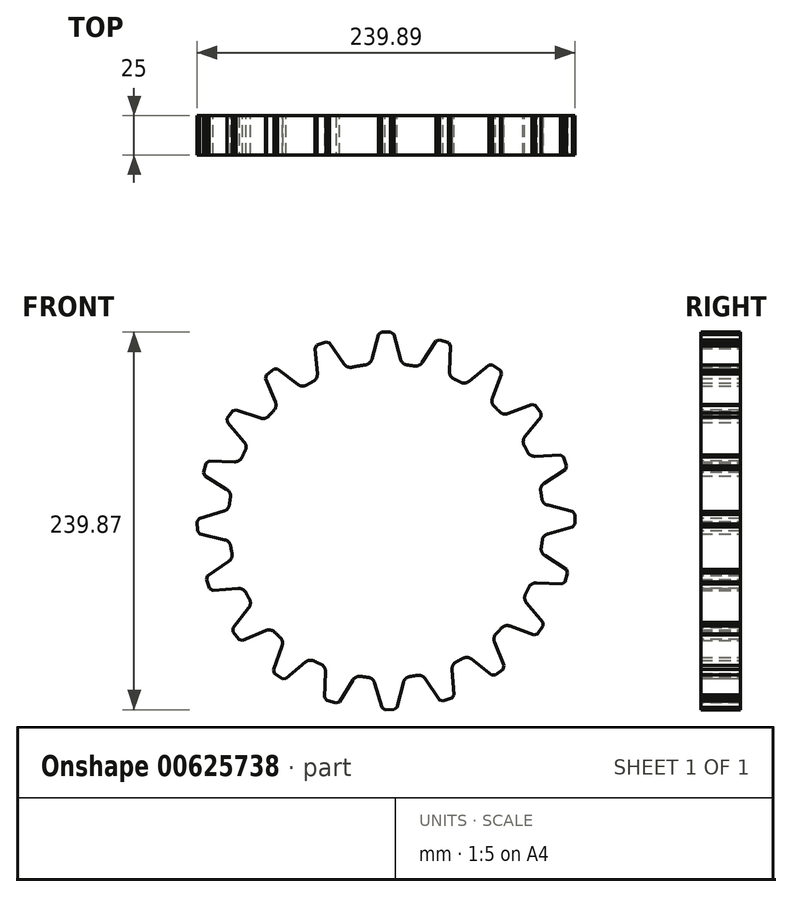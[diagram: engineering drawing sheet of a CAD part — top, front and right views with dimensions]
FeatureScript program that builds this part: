
annotation { "Feature Type Name" : "Feature", "Feature Type Description" : "" }
export const myFeature = defineFeature(function(context is Context, id is Id, definition is map)
    precondition{}
    {
        {
            var Q0;
            Q0=qCreatedBy(makeId("Front.planeOp"),FACE);
            var sketch = newSketch(context, id + "F0", { "sketchPlane" : qUnion([Q0])});
            skCircle(sketch, "E0", {"center": v(0, 0) * mm, "radius": 100 * mm});
            skCircle(sketch, "E1", {"center": v(0, 0) * mm, "radius": 120 * mm, "construction": true});
            skLineSegment(sketch, "E2", {"start": v(0, 0) * mm, "end": v(0, 133.33) * mm, "construction": true});
            skLineSegment(sketch, "E3", {"start": v(-4.5, 119.92) * mm, "end": v(-9.97, 99.5) * mm});
            skLineSegment(sketch, "E4.MirrorCS", {"start": v(4.5, 119.92) * mm, "end": v(9.97, 99.5) * mm});
            skLineSegment(sketch, "E5", {"start": v(-4.5, 119.92) * mm, "end": v(4.5, 119.92) * mm});
            skLineSegment(sketch, "E6.1.0", {"start": v(41.13, 112.73) * mm, "end": v(40.06, 91.62) * mm});
            skLineSegment(sketch, "E6.1.1", {"start": v(32.56, 115.5) * mm, "end": v(41.13, 112.73) * mm});
            skLineSegment(sketch, "E6.1.2", {"start": v(32.56, 115.5) * mm, "end": v(21.09, 97.75) * mm});
            skLineSegment(sketch, "E6.2.0", {"start": v(73.78, 94.64) * mm, "end": v(66.28, 74.88) * mm});
            skLineSegment(sketch, "E6.2.1", {"start": v(66.48, 99.9) * mm, "end": v(73.78, 94.64) * mm});
            skLineSegment(sketch, "E6.2.2", {"start": v(66.48, 99.9) * mm, "end": v(50.1, 86.54) * mm});
            skLineSegment(sketch, "E6.3.0", {"start": v(99.29, 67.4) * mm, "end": v(86.08, 50.9) * mm});
            skLineSegment(sketch, "E6.3.1", {"start": v(93.96, 74.64) * mm, "end": v(99.29, 67.4) * mm});
            skLineSegment(sketch, "E6.3.2", {"start": v(93.96, 74.64) * mm, "end": v(74.27, 66.96) * mm});
            skLineSegment(sketch, "E6.4.0", {"start": v(115.2, 33.62) * mm, "end": v(97.55, 21.98) * mm});
            skLineSegment(sketch, "E6.4.1", {"start": v(112.35, 42.16) * mm, "end": v(115.2, 33.62) * mm});
            skLineSegment(sketch, "E6.4.2", {"start": v(112.35, 42.16) * mm, "end": v(91.25, 40.9) * mm});
            skLineSegment(sketch, "E6.5.0", {"start": v(119.95, -3.4) * mm, "end": v(99.59, -9.06) * mm});
            skLineSegment(sketch, "E6.5.1", {"start": v(119.87, 5.6) * mm, "end": v(119.95, -3.4) * mm});
            skLineSegment(sketch, "E6.5.2", {"start": v(119.87, 5.6) * mm, "end": v(99.4, 10.88) * mm});
            skLineSegment(sketch, "E6.6.0", {"start": v(113.1, -40.1) * mm, "end": v(91.99, -39.22) * mm});
            skLineSegment(sketch, "E6.6.1", {"start": v(115.8, -31.5) * mm, "end": v(113.1, -40.1) * mm});
            skLineSegment(sketch, "E6.6.2", {"start": v(115.8, -31.5) * mm, "end": v(97.94, -20.19) * mm});
            skLineSegment(sketch, "E6.7.0", {"start": v(95.31, -72.9) * mm, "end": v(75.49, -65.59) * mm});
            skLineSegment(sketch, "E6.7.1", {"start": v(100.51, -65.56) * mm, "end": v(95.31, -72.9) * mm});
            skLineSegment(sketch, "E6.7.2", {"start": v(100.51, -65.56) * mm, "end": v(87, -49.3) * mm});
            skLineSegment(sketch, "E6.8.0", {"start": v(68.3, -98.67) * mm, "end": v(51.68, -85.6) * mm});
            skLineSegment(sketch, "E6.8.1", {"start": v(75.5, -93.27) * mm, "end": v(68.3, -98.67) * mm});
            skLineSegment(sketch, "E6.8.2", {"start": v(75.5, -93.27) * mm, "end": v(67.64, -73.65) * mm});
            skLineSegment(sketch, "E6.9.0", {"start": v(34.68, -114.88) * mm, "end": v(22.88, -97.35) * mm});
            skLineSegment(sketch, "E6.9.1", {"start": v(43.2, -111.96) * mm, "end": v(34.68, -114.88) * mm});
            skLineSegment(sketch, "E6.9.2", {"start": v(43.2, -111.96) * mm, "end": v(41.74, -90.87) * mm});
            skLineSegment(sketch, "E6.10.0", {"start": v(-2.3, -119.98) * mm, "end": v(-8.14, -99.67) * mm});
            skLineSegment(sketch, "E6.10.1", {"start": v(6.7, -119.81) * mm, "end": v(-2.3, -119.98) * mm});
            skLineSegment(sketch, "E6.10.2", {"start": v(6.7, -119.81) * mm, "end": v(11.8, -99.3) * mm});
            skLineSegment(sketch, "E6.11.0", {"start": v(-39.05, -113.47) * mm, "end": v(-38.37, -92.35) * mm});
            skLineSegment(sketch, "E6.11.1", {"start": v(-30.44, -116.08) * mm, "end": v(-39.05, -113.47) * mm});
            skLineSegment(sketch, "E6.11.2", {"start": v(-30.44, -116.08) * mm, "end": v(-19.29, -98.12) * mm});
            skLineSegment(sketch, "E6.12.0", {"start": v(-72.03, -95.98) * mm, "end": v(-64.89, -76.09) * mm});
            skLineSegment(sketch, "E6.12.1", {"start": v(-64.63, -101.1) * mm, "end": v(-72.03, -95.98) * mm});
            skLineSegment(sketch, "E6.12.2", {"start": v(-64.63, -101.1) * mm, "end": v(-48.5, -87.45) * mm});
            skLineSegment(sketch, "E6.13.0", {"start": v(-98.03, -69.2) * mm, "end": v(-85.13, -52.47) * mm});
            skLineSegment(sketch, "E6.13.1", {"start": v(-92.57, -76.36) * mm, "end": v(-98.03, -69.2) * mm});
            skLineSegment(sketch, "E6.13.2", {"start": v(-92.57, -76.36) * mm, "end": v(-73.03, -68.31) * mm});
            skLineSegment(sketch, "E6.14.0", {"start": v(-114.56, -35.73) * mm, "end": v(-97.13, -23.77) * mm});
            skLineSegment(sketch, "E6.14.1", {"start": v(-111.56, -44.22) * mm, "end": v(-114.56, -35.73) * mm});
            skLineSegment(sketch, "E6.14.2", {"start": v(-111.56, -44.22) * mm, "end": v(-90.49, -42.57) * mm});
            skLineSegment(sketch, "E6.15.0", {"start": v(-120, 1.2) * mm, "end": v(-99.74, 7.22) * mm});
            skLineSegment(sketch, "E6.15.1", {"start": v(-119.75, -7.8) * mm, "end": v(-120, 1.2) * mm});
            skLineSegment(sketch, "E6.15.2", {"start": v(-119.75, -7.8) * mm, "end": v(-99.19, -12.7) * mm});
            skLineSegment(sketch, "E6.16.0", {"start": v(-113.82, 38) * mm, "end": v(-92.7, 37.52) * mm});
            skLineSegment(sketch, "E6.16.1", {"start": v(-116.35, 29.37) * mm, "end": v(-113.82, 38) * mm});
            skLineSegment(sketch, "E6.16.2", {"start": v(-116.35, 29.37) * mm, "end": v(-98.3, 18.38) * mm});
            skLineSegment(sketch, "E6.17.0", {"start": v(-96.64, 71.14) * mm, "end": v(-76.68, 64.19) * mm});
            skLineSegment(sketch, "E6.17.1", {"start": v(-101.7, 63.7) * mm, "end": v(-96.64, 71.14) * mm});
            skLineSegment(sketch, "E6.17.2", {"start": v(-101.7, 63.7) * mm, "end": v(-87.9, 47.7) * mm});
            skLineSegment(sketch, "E6.18.0", {"start": v(-70.1, 97.4) * mm, "end": v(-53.25, 84.64) * mm});
            skLineSegment(sketch, "E6.18.1", {"start": v(-77.2, 91.87) * mm, "end": v(-70.1, 97.4) * mm});
            skLineSegment(sketch, "E6.18.2", {"start": v(-77.2, 91.87) * mm, "end": v(-68.98, 72.4) * mm});
            skLineSegment(sketch, "E6.19.0", {"start": v(-36.78, 114.22) * mm, "end": v(-24.66, 96.91) * mm});
            skLineSegment(sketch, "E6.19.1", {"start": v(-45.24, 111.14) * mm, "end": v(-36.78, 114.22) * mm});
            skLineSegment(sketch, "E6.19.2", {"start": v(-45.24, 111.14) * mm, "end": v(-43.4, 90.1) * mm});
            skLineSegment(sketch, "E6.anchor1", {"start": v(0, 0) * mm, "end": v(-9.97, 99.5) * mm, "construction": true});
            skLineSegment(sketch, "E6.anchor2", {"start": v(0, 0) * mm, "end": v(-43.4, 90.1) * mm, "construction": true});
            skSolve(sketch);
        }
        {
            var Q0;
            Q0 = qSketchRegion(id + "F0", true);
            extrude(context, id + "F1", {"entities" : qUnion([Q0]), "depth" : 25 * mm, "offsetDistance" : 25 * mm});
        }
        {
            var Q0;
            Q0=makeQuery(id+"F1.opExtrude","SWEPT_EDGE",EDGE,{"disambiguationData":[OSD([sQuery(id+"F0.wireOp",EDGE,"E4.MirrorCS"),sQuery(id+"F0.wireOp",EDGE,"E5")])]});
            var Q1;
            Q1=makeQuery(id+"F1.opExtrude","SWEPT_EDGE",EDGE,{"disambiguationData":[OSD([sQuery(id+"F0.wireOp",EDGE,"E3"),sQuery(id+"F0.wireOp",EDGE,"E5")])]});
            var Q2;
            Q2=makeQuery(id+"F1.opExtrude","SWEPT_EDGE",EDGE,{"disambiguationData":[OSD([sQuery(id+"F0.wireOp",EDGE,"E6.1.1"),sQuery(id+"F0.wireOp",EDGE,"E6.1.2")])]});
            var Q3;
            Q3=makeQuery(id+"F1.opExtrude","SWEPT_EDGE",EDGE,{"disambiguationData":[OSD([sQuery(id+"F0.wireOp",EDGE,"E6.1.0"),sQuery(id+"F0.wireOp",EDGE,"E6.1.1")])]});
            var Q4;
            Q4=makeQuery(id+"F1.opExtrude","SWEPT_EDGE",EDGE,{"disambiguationData":[OSD([sQuery(id+"F0.wireOp",EDGE,"E6.2.1"),sQuery(id+"F0.wireOp",EDGE,"E6.2.2")])]});
            var Q5;
            Q5=makeQuery(id+"F1.opExtrude","SWEPT_EDGE",EDGE,{"disambiguationData":[OSD([sQuery(id+"F0.wireOp",EDGE,"E6.2.0"),sQuery(id+"F0.wireOp",EDGE,"E6.2.1")])]});
            var Q6;
            Q6=makeQuery(id+"F1.opExtrude","SWEPT_EDGE",EDGE,{"disambiguationData":[OSD([sQuery(id+"F0.wireOp",EDGE,"E6.3.0"),sQuery(id+"F0.wireOp",EDGE,"E6.3.1")])]});
            var Q7;
            Q7=makeQuery(id+"F1.opExtrude","SWEPT_EDGE",EDGE,{"disambiguationData":[OSD([sQuery(id+"F0.wireOp",EDGE,"E6.3.1"),sQuery(id+"F0.wireOp",EDGE,"E6.3.2")])]});
            var Q8;
            Q8=makeQuery(id+"F1.opExtrude","SWEPT_EDGE",EDGE,{"disambiguationData":[OSD([sQuery(id+"F0.wireOp",EDGE,"E6.4.1"),sQuery(id+"F0.wireOp",EDGE,"E6.4.2")])]});
            var Q9;
            Q9=makeQuery(id+"F1.opExtrude","SWEPT_EDGE",EDGE,{"disambiguationData":[OSD([sQuery(id+"F0.wireOp",EDGE,"E6.4.0"),sQuery(id+"F0.wireOp",EDGE,"E6.4.1")])]});
            var Q10;
            Q10=makeQuery(id+"F1.opExtrude","SWEPT_EDGE",EDGE,{"disambiguationData":[OSD([sQuery(id+"F0.wireOp",EDGE,"E6.5.1"),sQuery(id+"F0.wireOp",EDGE,"E6.5.2")])]});
            var Q11;
            Q11=makeQuery(id+"F1.opExtrude","SWEPT_EDGE",EDGE,{"disambiguationData":[OSD([sQuery(id+"F0.wireOp",EDGE,"E6.5.0"),sQuery(id+"F0.wireOp",EDGE,"E6.5.1")])]});
            var Q12;
            Q12=makeQuery(id+"F1.opExtrude","SWEPT_EDGE",EDGE,{"disambiguationData":[OSD([sQuery(id+"F0.wireOp",EDGE,"E6.6.1"),sQuery(id+"F0.wireOp",EDGE,"E6.6.2")])]});
            var Q13;
            Q13=makeQuery(id+"F1.opExtrude","SWEPT_EDGE",EDGE,{"disambiguationData":[OSD([sQuery(id+"F0.wireOp",EDGE,"E6.6.0"),sQuery(id+"F0.wireOp",EDGE,"E6.6.1")])]});
            var Q14;
            Q14=makeQuery(id+"F1.opExtrude","SWEPT_EDGE",EDGE,{"disambiguationData":[OSD([sQuery(id+"F0.wireOp",EDGE,"E6.7.1"),sQuery(id+"F0.wireOp",EDGE,"E6.7.2")])]});
            var Q15;
            Q15=makeQuery(id+"F1.opExtrude","SWEPT_EDGE",EDGE,{"disambiguationData":[OSD([sQuery(id+"F0.wireOp",EDGE,"E6.7.0"),sQuery(id+"F0.wireOp",EDGE,"E6.7.1")])]});
            var Q16;
            Q16=makeQuery(id+"F1.opExtrude","SWEPT_EDGE",EDGE,{"disambiguationData":[OSD([sQuery(id+"F0.wireOp",EDGE,"E6.8.1"),sQuery(id+"F0.wireOp",EDGE,"E6.8.2")])]});
            var Q17;
            Q17=makeQuery(id+"F1.opExtrude","SWEPT_EDGE",EDGE,{"disambiguationData":[OSD([sQuery(id+"F0.wireOp",EDGE,"E6.8.0"),sQuery(id+"F0.wireOp",EDGE,"E6.8.1")])]});
            var Q18;
            Q18=makeQuery(id+"F1.opExtrude","SWEPT_EDGE",EDGE,{"disambiguationData":[OSD([sQuery(id+"F0.wireOp",EDGE,"E6.9.1"),sQuery(id+"F0.wireOp",EDGE,"E6.9.2")])]});
            var Q19;
            Q19=makeQuery(id+"F1.opExtrude","SWEPT_EDGE",EDGE,{"disambiguationData":[OSD([sQuery(id+"F0.wireOp",EDGE,"E6.9.0"),sQuery(id+"F0.wireOp",EDGE,"E6.9.1")])]});
            var Q20;
            Q20=makeQuery(id+"F1.opExtrude","SWEPT_EDGE",EDGE,{"disambiguationData":[OSD([sQuery(id+"F0.wireOp",EDGE,"E6.10.1"),sQuery(id+"F0.wireOp",EDGE,"E6.10.2")])]});
            var Q21;
            Q21=makeQuery(id+"F1.opExtrude","SWEPT_EDGE",EDGE,{"disambiguationData":[OSD([sQuery(id+"F0.wireOp",EDGE,"E6.10.0"),sQuery(id+"F0.wireOp",EDGE,"E6.10.1")])]});
            var Q22;
            Q22=makeQuery(id+"F1.opExtrude","SWEPT_EDGE",EDGE,{"disambiguationData":[OSD([sQuery(id+"F0.wireOp",EDGE,"E6.11.1"),sQuery(id+"F0.wireOp",EDGE,"E6.11.2")])]});
            var Q23;
            Q23=makeQuery(id+"F1.opExtrude","SWEPT_EDGE",EDGE,{"disambiguationData":[OSD([sQuery(id+"F0.wireOp",EDGE,"E6.11.0"),sQuery(id+"F0.wireOp",EDGE,"E6.11.1")])]});
            var Q24;
            Q24=makeQuery(id+"F1.opExtrude","SWEPT_EDGE",EDGE,{"disambiguationData":[OSD([sQuery(id+"F0.wireOp",EDGE,"E6.12.1"),sQuery(id+"F0.wireOp",EDGE,"E6.12.2")])]});
            var Q25;
            Q25=makeQuery(id+"F1.opExtrude","SWEPT_EDGE",EDGE,{"disambiguationData":[OSD([sQuery(id+"F0.wireOp",EDGE,"E6.12.0"),sQuery(id+"F0.wireOp",EDGE,"E6.12.1")])]});
            var Q26;
            Q26=makeQuery(id+"F1.opExtrude","SWEPT_EDGE",EDGE,{"disambiguationData":[OSD([sQuery(id+"F0.wireOp",EDGE,"E6.13.1"),sQuery(id+"F0.wireOp",EDGE,"E6.13.2")])]});
            var Q27;
            Q27=makeQuery(id+"F1.opExtrude","SWEPT_EDGE",EDGE,{"disambiguationData":[OSD([sQuery(id+"F0.wireOp",EDGE,"E6.13.0"),sQuery(id+"F0.wireOp",EDGE,"E6.13.1")])]});
            var Q28;
            Q28=makeQuery(id+"F1.opExtrude","SWEPT_EDGE",EDGE,{"disambiguationData":[OSD([sQuery(id+"F0.wireOp",EDGE,"E6.14.1"),sQuery(id+"F0.wireOp",EDGE,"E6.14.2")])]});
            var Q29;
            Q29=makeQuery(id+"F1.opExtrude","SWEPT_EDGE",EDGE,{"disambiguationData":[OSD([sQuery(id+"F0.wireOp",EDGE,"E6.14.0"),sQuery(id+"F0.wireOp",EDGE,"E6.14.1")])]});
            var Q30;
            Q30=makeQuery(id+"F1.opExtrude","SWEPT_EDGE",EDGE,{"disambiguationData":[OSD([sQuery(id+"F0.wireOp",EDGE,"E6.15.1"),sQuery(id+"F0.wireOp",EDGE,"E6.15.2")])]});
            var Q31;
            Q31=makeQuery(id+"F1.opExtrude","SWEPT_EDGE",EDGE,{"disambiguationData":[OSD([sQuery(id+"F0.wireOp",EDGE,"E6.15.0"),sQuery(id+"F0.wireOp",EDGE,"E6.15.1")])]});
            var Q32;
            Q32=makeQuery(id+"F1.opExtrude","SWEPT_EDGE",EDGE,{"disambiguationData":[OSD([sQuery(id+"F0.wireOp",EDGE,"E6.16.1"),sQuery(id+"F0.wireOp",EDGE,"E6.16.2")])]});
            var Q33;
            Q33=makeQuery(id+"F1.opExtrude","SWEPT_EDGE",EDGE,{"disambiguationData":[OSD([sQuery(id+"F0.wireOp",EDGE,"E6.16.0"),sQuery(id+"F0.wireOp",EDGE,"E6.16.1")])]});
            var Q34;
            Q34=makeQuery(id+"F1.opExtrude","SWEPT_EDGE",EDGE,{"disambiguationData":[OSD([sQuery(id+"F0.wireOp",EDGE,"E6.17.1"),sQuery(id+"F0.wireOp",EDGE,"E6.17.2")])]});
            var Q35;
            Q35=makeQuery(id+"F1.opExtrude","SWEPT_EDGE",EDGE,{"disambiguationData":[OSD([sQuery(id+"F0.wireOp",EDGE,"E6.17.0"),sQuery(id+"F0.wireOp",EDGE,"E6.17.1")])]});
            var Q36;
            Q36=makeQuery(id+"F1.opExtrude","SWEPT_EDGE",EDGE,{"disambiguationData":[OSD([sQuery(id+"F0.wireOp",EDGE,"E6.18.1"),sQuery(id+"F0.wireOp",EDGE,"E6.18.2")])]});
            var Q37;
            Q37=makeQuery(id+"F1.opExtrude","SWEPT_EDGE",EDGE,{"disambiguationData":[OSD([sQuery(id+"F0.wireOp",EDGE,"E6.18.0"),sQuery(id+"F0.wireOp",EDGE,"E6.18.1")])]});
            var Q38;
            Q38=makeQuery(id+"F1.opExtrude","SWEPT_EDGE",EDGE,{"disambiguationData":[OSD([sQuery(id+"F0.wireOp",EDGE,"E6.19.1"),sQuery(id+"F0.wireOp",EDGE,"E6.19.2")])]});
            var Q39;
            Q39=makeQuery(id+"F1.opExtrude","SWEPT_EDGE",EDGE,{"disambiguationData":[OSD([sQuery(id+"F0.wireOp",EDGE,"E6.19.0"),sQuery(id+"F0.wireOp",EDGE,"E6.19.1")])]});
            chamfer(context, id + "F2", {"entities" : qUnion([Q0, Q1, Q2, Q3, Q4, Q5, Q6, Q7, Q8, Q9, Q10, Q11, Q12, Q13, Q14, Q15, Q16, Q17, Q18, Q19, Q20, Q21, Q22, Q23, Q24, Q25, Q26, Q27, Q28, Q29, Q30, Q31, Q32, Q33, Q34, Q35, Q36, Q37, Q38, Q39]), "width" : 2 * mm, "tangentPropagation" : true});
        }
        {
            var Q0;
            Q0=makeQuery(id+"F1.opExtrude","SWEPT_EDGE",EDGE,{"disambiguationData":[OSD([sQuery(id+"F0.wireOp",EDGE,"E0"),sQuery(id+"F0.wireOp",EDGE,"E6.18.0")])]});
            var Q1;
            Q1=makeQuery(id+"F1.opExtrude","SWEPT_EDGE",EDGE,{"disambiguationData":[OSD([sQuery(id+"F0.wireOp",EDGE,"E0"),sQuery(id+"F0.wireOp",EDGE,"E6.19.2")])]});
            var Q2;
            Q2=makeQuery(id+"F1.opExtrude","SWEPT_EDGE",EDGE,{"disambiguationData":[OSD([sQuery(id+"F0.wireOp",EDGE,"E0"),sQuery(id+"F0.wireOp",EDGE,"E6.19.0")])]});
            var Q3;
            Q3=makeQuery(id+"F1.opExtrude","SWEPT_EDGE",EDGE,{"disambiguationData":[OSD([sQuery(id+"F0.wireOp",EDGE,"E0"),sQuery(id+"F0.wireOp",EDGE,"E3")])]});
            var Q4;
            Q4=makeQuery(id+"F1.opExtrude","SWEPT_EDGE",EDGE,{"disambiguationData":[OSD([sQuery(id+"F0.wireOp",EDGE,"E0"),sQuery(id+"F0.wireOp",EDGE,"E4.MirrorCS")])]});
            var Q5;
            Q5=makeQuery(id+"F1.opExtrude","SWEPT_EDGE",EDGE,{"disambiguationData":[OSD([sQuery(id+"F0.wireOp",EDGE,"E0"),sQuery(id+"F0.wireOp",EDGE,"E6.1.2")])]});
            var Q6;
            Q6=makeQuery(id+"F1.opExtrude","SWEPT_EDGE",EDGE,{"disambiguationData":[OSD([sQuery(id+"F0.wireOp",EDGE,"E0"),sQuery(id+"F0.wireOp",EDGE,"E6.1.0")])]});
            var Q7;
            Q7=makeQuery(id+"F1.opExtrude","SWEPT_EDGE",EDGE,{"disambiguationData":[OSD([sQuery(id+"F0.wireOp",EDGE,"E0"),sQuery(id+"F0.wireOp",EDGE,"E6.2.2")])]});
            var Q8;
            Q8=makeQuery(id+"F1.opExtrude","SWEPT_EDGE",EDGE,{"disambiguationData":[OSD([sQuery(id+"F0.wireOp",EDGE,"E0"),sQuery(id+"F0.wireOp",EDGE,"E6.2.0")])]});
            var Q9;
            Q9=makeQuery(id+"F1.opExtrude","SWEPT_EDGE",EDGE,{"disambiguationData":[OSD([sQuery(id+"F0.wireOp",EDGE,"E0"),sQuery(id+"F0.wireOp",EDGE,"E6.3.2")])]});
            var Q10;
            Q10=makeQuery(id+"F1.opExtrude","SWEPT_EDGE",EDGE,{"disambiguationData":[OSD([sQuery(id+"F0.wireOp",EDGE,"E0"),sQuery(id+"F0.wireOp",EDGE,"E6.3.0")])]});
            var Q11;
            Q11=makeQuery(id+"F1.opExtrude","SWEPT_EDGE",EDGE,{"disambiguationData":[OSD([sQuery(id+"F0.wireOp",EDGE,"E0"),sQuery(id+"F0.wireOp",EDGE,"E6.4.2")])]});
            var Q12;
            Q12=makeQuery(id+"F1.opExtrude","SWEPT_EDGE",EDGE,{"disambiguationData":[OSD([sQuery(id+"F0.wireOp",EDGE,"E0"),sQuery(id+"F0.wireOp",EDGE,"E6.4.0")])]});
            var Q13;
            Q13=makeQuery(id+"F1.opExtrude","SWEPT_EDGE",EDGE,{"disambiguationData":[OSD([sQuery(id+"F0.wireOp",EDGE,"E0"),sQuery(id+"F0.wireOp",EDGE,"E6.5.2")])]});
            var Q14;
            Q14=makeQuery(id+"F1.opExtrude","SWEPT_EDGE",EDGE,{"disambiguationData":[OSD([sQuery(id+"F0.wireOp",EDGE,"E0"),sQuery(id+"F0.wireOp",EDGE,"E6.5.0")])]});
            var Q15;
            Q15=makeQuery(id+"F1.opExtrude","SWEPT_EDGE",EDGE,{"disambiguationData":[OSD([sQuery(id+"F0.wireOp",EDGE,"E0"),sQuery(id+"F0.wireOp",EDGE,"E6.6.2")])]});
            var Q16;
            Q16=makeQuery(id+"F1.opExtrude","SWEPT_EDGE",EDGE,{"disambiguationData":[OSD([sQuery(id+"F0.wireOp",EDGE,"E0"),sQuery(id+"F0.wireOp",EDGE,"E6.6.0")])]});
            var Q17;
            Q17=makeQuery(id+"F1.opExtrude","SWEPT_EDGE",EDGE,{"disambiguationData":[OSD([sQuery(id+"F0.wireOp",EDGE,"E0"),sQuery(id+"F0.wireOp",EDGE,"E6.7.2")])]});
            var Q18;
            Q18=makeQuery(id+"F1.opExtrude","SWEPT_EDGE",EDGE,{"disambiguationData":[OSD([sQuery(id+"F0.wireOp",EDGE,"E0"),sQuery(id+"F0.wireOp",EDGE,"E6.7.0")])]});
            var Q19;
            Q19=makeQuery(id+"F1.opExtrude","SWEPT_EDGE",EDGE,{"disambiguationData":[OSD([sQuery(id+"F0.wireOp",EDGE,"E0"),sQuery(id+"F0.wireOp",EDGE,"E6.8.2")])]});
            var Q20;
            Q20=makeQuery(id+"F1.opExtrude","SWEPT_EDGE",EDGE,{"disambiguationData":[OSD([sQuery(id+"F0.wireOp",EDGE,"E0"),sQuery(id+"F0.wireOp",EDGE,"E6.8.0")])]});
            var Q21;
            Q21=makeQuery(id+"F1.opExtrude","SWEPT_EDGE",EDGE,{"disambiguationData":[OSD([sQuery(id+"F0.wireOp",EDGE,"E0"),sQuery(id+"F0.wireOp",EDGE,"E6.9.2")])]});
            var Q22;
            Q22=makeQuery(id+"F1.opExtrude","SWEPT_EDGE",EDGE,{"disambiguationData":[OSD([sQuery(id+"F0.wireOp",EDGE,"E0"),sQuery(id+"F0.wireOp",EDGE,"E6.9.0")])]});
            var Q23;
            Q23=makeQuery(id+"F1.opExtrude","SWEPT_EDGE",EDGE,{"disambiguationData":[OSD([sQuery(id+"F0.wireOp",EDGE,"E0"),sQuery(id+"F0.wireOp",EDGE,"E6.10.2")])]});
            var Q24;
            Q24=makeQuery(id+"F1.opExtrude","SWEPT_EDGE",EDGE,{"disambiguationData":[OSD([sQuery(id+"F0.wireOp",EDGE,"E0"),sQuery(id+"F0.wireOp",EDGE,"E6.10.0")])]});
            var Q25;
            Q25=makeQuery(id+"F1.opExtrude","SWEPT_EDGE",EDGE,{"disambiguationData":[OSD([sQuery(id+"F0.wireOp",EDGE,"E0"),sQuery(id+"F0.wireOp",EDGE,"E6.11.2")])]});
            var Q26;
            Q26=makeQuery(id+"F1.opExtrude","SWEPT_EDGE",EDGE,{"disambiguationData":[OSD([sQuery(id+"F0.wireOp",EDGE,"E0"),sQuery(id+"F0.wireOp",EDGE,"E6.11.0")])]});
            var Q27;
            Q27=makeQuery(id+"F1.opExtrude","SWEPT_EDGE",EDGE,{"disambiguationData":[OSD([sQuery(id+"F0.wireOp",EDGE,"E0"),sQuery(id+"F0.wireOp",EDGE,"E6.12.2")])]});
            var Q28;
            Q28=makeQuery(id+"F1.opExtrude","SWEPT_EDGE",EDGE,{"disambiguationData":[OSD([sQuery(id+"F0.wireOp",EDGE,"E0"),sQuery(id+"F0.wireOp",EDGE,"E6.12.0")])]});
            var Q29;
            Q29=makeQuery(id+"F1.opExtrude","SWEPT_EDGE",EDGE,{"disambiguationData":[OSD([sQuery(id+"F0.wireOp",EDGE,"E0"),sQuery(id+"F0.wireOp",EDGE,"E6.13.2")])]});
            var Q30;
            Q30=makeQuery(id+"F1.opExtrude","SWEPT_EDGE",EDGE,{"disambiguationData":[OSD([sQuery(id+"F0.wireOp",EDGE,"E0"),sQuery(id+"F0.wireOp",EDGE,"E6.13.0")])]});
            var Q31;
            Q31=makeQuery(id+"F1.opExtrude","SWEPT_EDGE",EDGE,{"disambiguationData":[OSD([sQuery(id+"F0.wireOp",EDGE,"E0"),sQuery(id+"F0.wireOp",EDGE,"E6.14.2")])]});
            var Q32;
            Q32=makeQuery(id+"F1.opExtrude","SWEPT_EDGE",EDGE,{"disambiguationData":[OSD([sQuery(id+"F0.wireOp",EDGE,"E0"),sQuery(id+"F0.wireOp",EDGE,"E6.14.0")])]});
            var Q33;
            Q33=makeQuery(id+"F1.opExtrude","SWEPT_EDGE",EDGE,{"disambiguationData":[OSD([sQuery(id+"F0.wireOp",EDGE,"E0"),sQuery(id+"F0.wireOp",EDGE,"E6.15.2")])]});
            var Q34;
            Q34=makeQuery(id+"F1.opExtrude","SWEPT_EDGE",EDGE,{"disambiguationData":[OSD([sQuery(id+"F0.wireOp",EDGE,"E0"),sQuery(id+"F0.wireOp",EDGE,"E6.15.0")])]});
            var Q35;
            Q35=makeQuery(id+"F1.opExtrude","SWEPT_EDGE",EDGE,{"disambiguationData":[OSD([sQuery(id+"F0.wireOp",EDGE,"E0"),sQuery(id+"F0.wireOp",EDGE,"E6.16.2")])]});
            var Q36;
            Q36=makeQuery(id+"F1.opExtrude","SWEPT_EDGE",EDGE,{"disambiguationData":[OSD([sQuery(id+"F0.wireOp",EDGE,"E0"),sQuery(id+"F0.wireOp",EDGE,"E6.16.0")])]});
            var Q37;
            Q37=makeQuery(id+"F1.opExtrude","SWEPT_EDGE",EDGE,{"disambiguationData":[OSD([sQuery(id+"F0.wireOp",EDGE,"E0"),sQuery(id+"F0.wireOp",EDGE,"E6.17.2")])]});
            var Q38;
            Q38=makeQuery(id+"F1.opExtrude","SWEPT_EDGE",EDGE,{"disambiguationData":[OSD([sQuery(id+"F0.wireOp",EDGE,"E0"),sQuery(id+"F0.wireOp",EDGE,"E6.17.0")])]});
            var Q39;
            Q39=makeQuery(id+"F1.opExtrude","SWEPT_EDGE",EDGE,{"disambiguationData":[OSD([sQuery(id+"F0.wireOp",EDGE,"E0"),sQuery(id+"F0.wireOp",EDGE,"E6.18.2")])]});
            fillet(context, id + "F3", {"entities" : qUnion([Q0, Q1, Q2, Q3, Q4, Q5, Q6, Q7, Q8, Q9, Q10, Q11, Q12, Q13, Q14, Q15, Q16, Q17, Q18, Q19, Q20, Q21, Q22, Q23, Q24, Q25, Q26, Q27, Q28, Q29, Q30, Q31, Q32, Q33, Q34, Q35, Q36, Q37, Q38, Q39]), "radius" : 5 * mm, "tangentPropagation" : true, "allowEdgeOverflow" : false});
        }
    });
